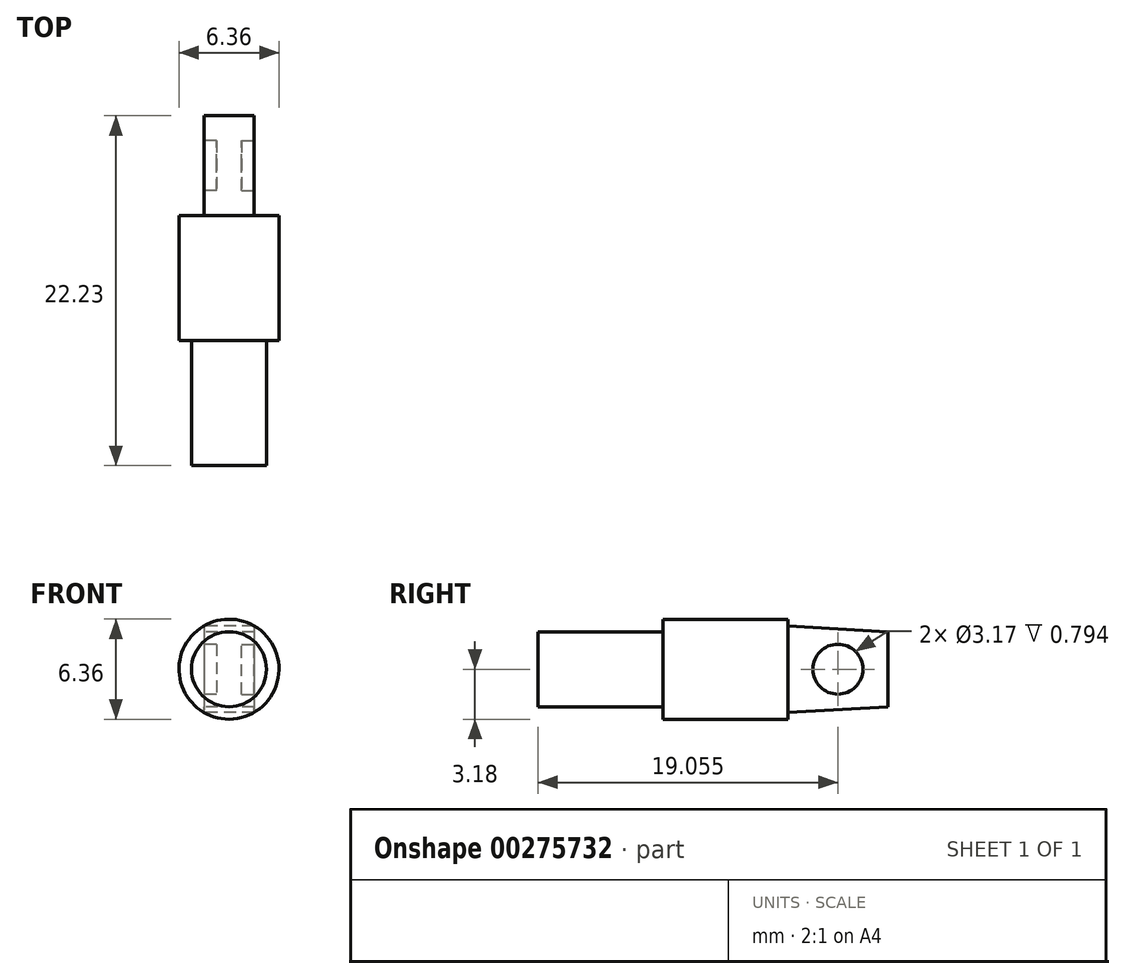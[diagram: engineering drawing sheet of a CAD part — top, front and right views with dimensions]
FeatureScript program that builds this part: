
annotation { "Feature Type Name" : "Feature", "Feature Type Description" : "" }
export const myFeature = defineFeature(function(context is Context, id is Id, definition is map)
    precondition{}
    {
        {
            var Q0;
            Q0=qCreatedBy(makeId("Front.planeOp"),FACE);
            var sketch = newSketch(context, id + "F0", { "sketchPlane" : qUnion([Q0])});
            skCircle(sketch, "E0", {"center": v(0, 0) * mm, "radius": 3.18 * mm});
            skCircle(sketch, "E1", {"center": v(0, 0) * mm, "radius": 2.38 * mm});
            skSolve(sketch);
        }
        {
            var Q0;
            Q0=qSketchRegion(id+"F0",true);
            extrude(context, id + "F1", {"entities" : qUnion([Q0]), "depth" : 7.94 * mm});
        }
        {
            var Q0;
            Q0=makeQuery(id+"F0.imprint","IMPRINT",FACE,{"disambiguationData":[TD([[makeQuery(id+"F0.imprint","IMPRINT",EDGE,{"derivedFrom":sQuery(id+"F0.wireOp",EDGE,"E1")}),1.0]])]});
            extrude(context, id + "F2", {"entities" : qUnion([Q0]), "operationType" : NewBodyOperationType.ADD, "depth" : 15.88 * mm});
        }
        {
            var Q0;
            {var subQ0=sQuery(id+"F0.wireOp",EDGE,"E1");Q0=makeQuery(id+"F2.boolean.opBoolean","MERGE",FACE,{"derivedFrom":[makeQuery(id+"F1.opExtrude","CAP_FACE",FACE,{"disambiguationData":[OSD([sQuery(id+"F0.wireOp",EDGE,"E0"),subQ0])],"isStart":true}),makeQuery(id+"F2.opExtrude","CAP_FACE",FACE,{"disambiguationData":[OSD([subQ0])],"isStart":true})]});}
            var sketch = newSketch(context, id + "F3", { "sketchPlane" : qUnion([Q0])});
            skPoint(sketch, "E2.middle", {"position": v(0, 0) * mm});
            skLineSegment(sketch, "E3.bottom", {"start": v(-1.59, 2.75) * mm, "end": v(1.59, 2.75) * mm});
            skLineSegment(sketch, "E3.top", {"start": v(-1.59, -2.75) * mm, "end": v(1.59, -2.75) * mm});
            skLineSegment(sketch, "E3.left", {"start": v(-1.59, 2.75) * mm, "end": v(-1.59, -2.75) * mm});
            skLineSegment(sketch, "E3.right", {"start": v(1.59, 2.75) * mm, "end": v(1.59, -2.75) * mm});
            skSolve(sketch);
        }
        {
            var Q0;
            Q0=makeQuery(id+"F3.imprint","IMPRINT",FACE,{"disambiguationData":[TD([[makeQuery(id+"F3.imprint","IMPRINT",EDGE,{"derivedFrom":sQuery(id+"F3.wireOp",EDGE,"E3.bottom")}),-1.0]])]});
            cPlane(context, id + "F4", {"entities" : qUnion([Q0]), "cplaneType" : CPlaneType.OFFSET, "offset" : 6.35 * mm, "width" : 152.4 * mm, "height" : 152.4 * mm});
        }
        {
            var Q0;
            Q0=qCreatedBy(id+"F4.planeOp",FACE);
            var sketch = newSketch(context, id + "F5", { "sketchPlane" : qUnion([Q0])});
            skLineSegment(sketch, "E4.bottom", {"start": v(-1.59, 2.38) * mm, "end": v(1.59, 2.38) * mm});
            skLineSegment(sketch, "E4.top", {"start": v(-1.59, -2.38) * mm, "end": v(1.59, -2.38) * mm});
            skLineSegment(sketch, "E4.left", {"start": v(-1.59, 2.38) * mm, "end": v(-1.59, -2.38) * mm});
            skLineSegment(sketch, "E4.right", {"start": v(1.59, 2.38) * mm, "end": v(1.59, -2.38) * mm});
            skPoint(sketch, "E4.middle", {"position": v(0, 0) * mm});
            skSolve(sketch);
        }
        {
            var Q1;
            Q1=makeQuery(id+"F3.imprint","IMPRINT",FACE,{"disambiguationData":[TD([[makeQuery(id+"F3.imprint","IMPRINT",EDGE,{"derivedFrom":sQuery(id+"F3.wireOp",EDGE,"E3.bottom")}),-1.0]])]});
            var Q2;
            Q2=makeQuery(id+"F5.imprint","IMPRINT",FACE,{"disambiguationData":[TD([[makeQuery(id+"F5.imprint","IMPRINT",EDGE,{"derivedFrom":sQuery(id+"F5.wireOp",EDGE,"E4.bottom")}),-1.0]])]});
            loft(context, id + "F6", {"operationType" : NewBodyOperationType.ADD, "sheetProfilesArray" : [{ "sheetProfileEntities" : qUnion([Q1]) }, { "sheetProfileEntities" : qUnion([Q2]) }]});
        }
        {
            var Q0;
            Q0=makeQuery(id+"F6.opLoft","SWEPT_FACE",FACE,{"disambiguationData":[OSD([sQuery(id+"F0.wireOp",EDGE,"E0"),sQuery(id+"F3.wireOp",EDGE,"E3.bottom"),sQuery(id+"F3.wireOp",EDGE,"E3.top"),sQuery(id+"F3.wireOp",EDGE,"E3.left"),sQuery(id+"F5.wireOp",EDGE,"E4.bottom"),sQuery(id+"F5.wireOp",EDGE,"E4.top"),sQuery(id+"F5.wireOp",EDGE,"E4.left")])]});
            var sketch = newSketch(context, id + "F7", { "sketchPlane" : qUnion([Q0])});
            skPoint(sketch, "E5.centerSnap0", {"position": v(6.35, 0) * mm});
            skCircle(sketch, "E6", {"center": v(3.18, 0) * mm, "radius": 1.59 * mm});
            skSolve(sketch);
        }
        {
            var Q0;
            Q0=makeQuery(id+"F7.imprint","IMPRINT",FACE,{"disambiguationData":[TD([[makeQuery(id+"F7.imprint","IMPRINT",EDGE,{"derivedFrom":sQuery(id+"F7.wireOp",EDGE,"E6")}),1.0]])]});
            extrude(context, id + "F8", {"entities" : qUnion([Q0]), "operationType" : NewBodyOperationType.REMOVE, "oppositeDirection" : true, "depth" : 0.8 * mm});
        }
        {
            var Q0;
            Q0=makeQuery(id+"F6.opLoft","SWEPT_FACE",FACE,{"disambiguationData":[OSD([sQuery(id+"F0.wireOp",EDGE,"E0"),sQuery(id+"F3.wireOp",EDGE,"E3.bottom"),sQuery(id+"F3.wireOp",EDGE,"E3.top"),sQuery(id+"F3.wireOp",EDGE,"E3.right"),sQuery(id+"F5.wireOp",EDGE,"E4.bottom"),sQuery(id+"F5.wireOp",EDGE,"E4.top"),sQuery(id+"F5.wireOp",EDGE,"E4.right")])]});
            var sketch = newSketch(context, id + "F9", { "sketchPlane" : qUnion([Q0])});
            skCircle(sketch, "E7", {"center": v(-3.18, 0) * mm, "radius": 1.59 * mm});
            skPoint(sketch, "E7.centerSnap0", {"position": v(-6.35, 0) * mm});
            skSolve(sketch);
        }
        {
            var Q0;
            Q0=qSketchRegion(id+"F9",true);
            extrude(context, id + "F10", {"entities" : qUnion([Q0]), "operationType" : NewBodyOperationType.REMOVE, "oppositeDirection" : true, "depth" : 0.8 * mm});
        }
    });
